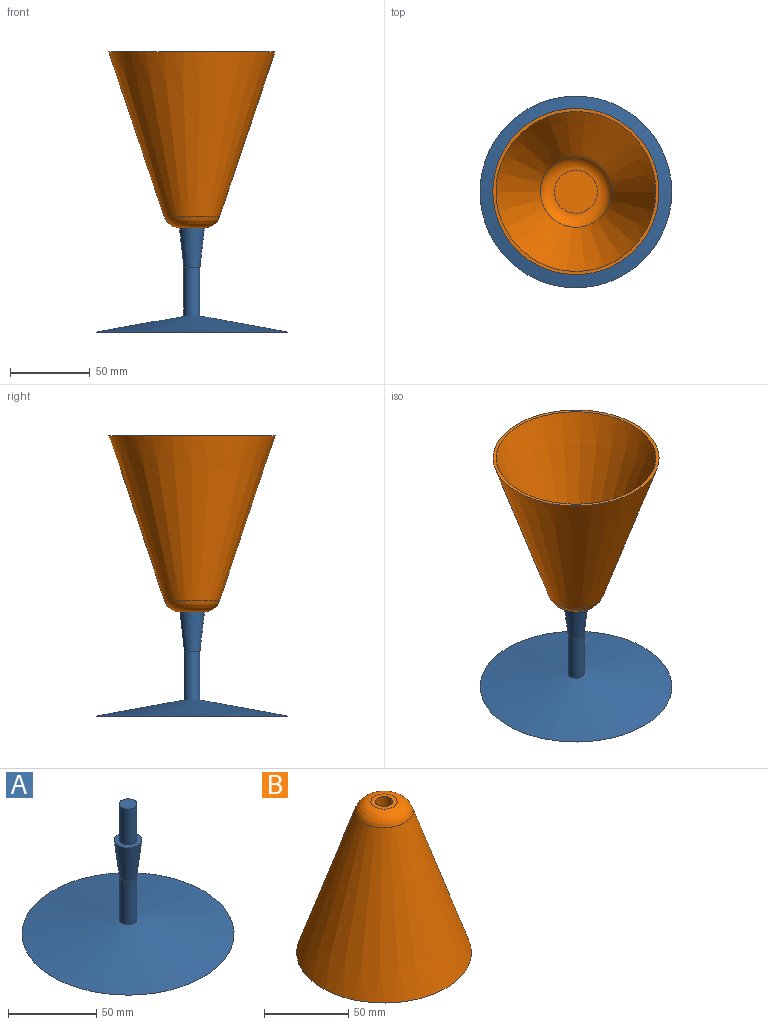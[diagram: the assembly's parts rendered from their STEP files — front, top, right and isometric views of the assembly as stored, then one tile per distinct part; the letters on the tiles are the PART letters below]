
ASSEMBLY  parts=2 mates=1
PART A: 7 faces, bbox 120x120x90 mm
  f0: cylinder r=5mm len=30.25mm, axis (0,0,-1), area 950.3mm2, adj f2,f4
  f1: plane 120x120mm, normal (0,0,-1), area 11309.7mm2, adj f2
  f2: cone r=60mm half-angle=79.7deg, axis (0,0,-1), area 11415.3mm2, adj f0,f1
  f3: plane 15.6x15.6mm, normal (0,0,1), area 112.6mm2, adj f4,f6
  f4: cone r=5mm half-angle=6.4deg, axis (0,0,1), area 1011.6mm2, adj f0,f3
  f5: plane 10x10mm, normal (0,0,1), area 78.5mm2, adj f6
  f6: cylinder r=5mm len=24.75mm, axis (0,0,-1), area 777.5mm2, adj f3,f5
PART B: 9 faces, bbox 104x104x110 mm
  f0: plane 104x104mm, normal (0,0,-1), area 640.9mm2, adj f2,f4
  f1: plane 15.63x15.63mm, normal (0,0,1), area 109.3mm2, adj f5,f7
  f2: cone r=52mm half-angle=18.6deg, axis (0,0,-1), area 23699.2mm2, adj f0,f7
  f3: plane 26.97x26.97mm, normal (0,0,-1), area 571.4mm2, adj f8
  f4: cone r=20mm half-angle=20.6deg, axis (0,0,-1), area 17923.8mm2, adj f0,f8
  f5: cylinder r=5.12mm len=25mm, axis (0,0,1), area 805mm2, adj f1,f6
  f6: plane 10.25x10.25mm, normal (0,0,1), area 82.5mm2, adj f5
  f7: torus R=7.81mm, axis (0,0,1), area 1039.8mm2, adj f1,f2
  f8: torus R=13.49mm, axis (0,0,1), area 1325.6mm2, adj f3,f4
PLACE A rot(axis=(0,-1,0),0deg) t=(9.19,24.32,110.18)mm
PLACE B rot(axis=(0,1,0),180deg) t=(9.19,24.32,285.43)mm
MATE fastened A.f0 <-> B.f2  axis (0,0,1) through (9.19,24.32,175.43)mm
